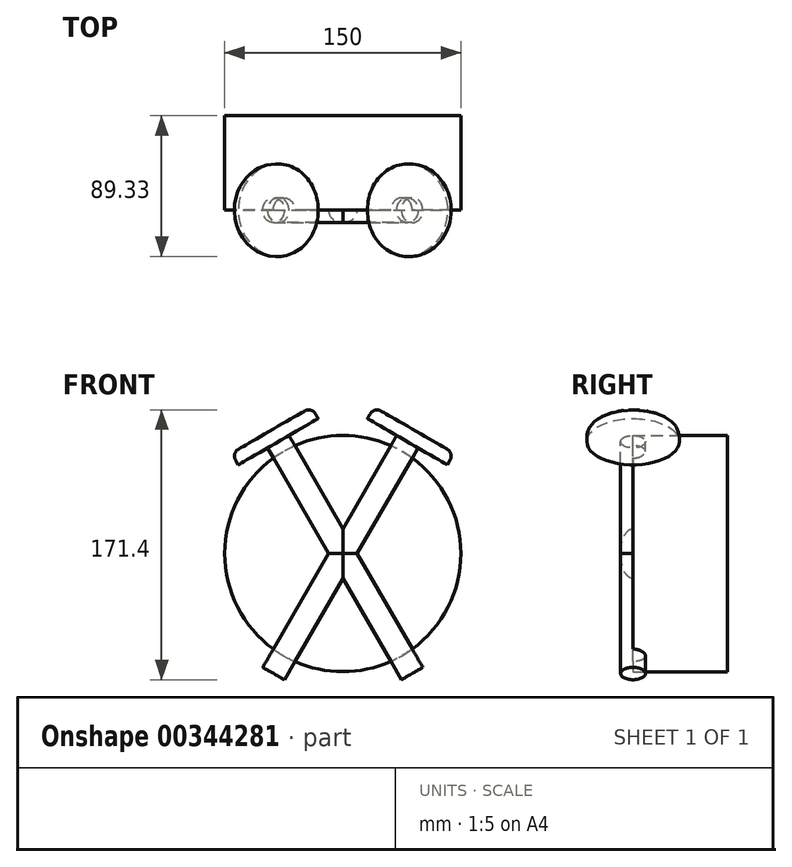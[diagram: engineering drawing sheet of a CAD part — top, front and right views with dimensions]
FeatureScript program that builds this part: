
annotation { "Feature Type Name" : "Feature", "Feature Type Description" : "" }
export const myFeature = defineFeature(function(context is Context, id is Id, definition is map)
    precondition{}
    {
        {
            var Q0;
            Q0=qCreatedBy(makeId("Front.planeOp"),FACE);
            var sketch = newSketch(context, id + "F0", { "sketchPlane" : qUnion([Q0])});
            skCircle(sketch, "E0", {"center": v(0, 0) * mm, "radius": 75 * mm});
            skSolve(sketch);
        }
        {
            var Q0;
            Q0 = qSketchRegion(id + "F0", true);
            var Q1;
            Q1=makeQuery(id+"F0.imprint","IMPRINT",FACE,{"disambiguationData":[TD([[makeQuery(id+"F0.imprint","IMPRINT",EDGE,{"derivedFrom":sQuery(id+"F0.wireOp",EDGE,"E0")}),1.0]])]});
            extrude(context, id + "F1", {"entities" : qUnion([Q0, Q1]), "depth" : 60 * mm});
        }
        {
            var Q0;
            Q0=makeQuery(id+"F1.opExtrude","CAP_FACE",FACE,{"disambiguationData":[OSD([sQuery(id+"F0.wireOp",EDGE,"E0")])],"isStart":false});
            var sketch = newSketch(context, id + "F2", { "sketchPlane" : qUnion([Q0])});
            skCircle(sketch, "E1", {"center": v(1.94, 0) * mm, "radius": 70 * mm});
            skSolve(sketch);
        }
        {
            var Q0;
            Q0=makeQuery(id+"F2.imprint","IMPRINT",FACE,{"disambiguationData":[TD([[makeQuery(id+"F2.imprint","IMPRINT",EDGE,{"derivedFrom":sQuery(id+"F2.wireOp",EDGE,"E1")}),-1.0]])]});
            var sketch = newSketch(context, id + "F3", { "sketchPlane" : qUnion([Q0])});
            skLineSegment(sketch, "E2.bottom", {"start": v(0, 82.05) * mm, "end": v(7.89, 82.05) * mm});
            skLineSegment(sketch, "E2.top", {"start": v(0, -87.98) * mm, "end": v(7.89, -87.98) * mm});
            skLineSegment(sketch, "E2.left", {"start": v(0, 82.05) * mm, "end": v(0, -87.98) * mm});
            skLineSegment(sketch, "E2.right", {"start": v(7.89, 82.05) * mm, "end": v(7.89, -87.98) * mm});
            skLineSegment(sketch, "E3.bottom", {"start": v(0, 82.05) * mm, "end": v(29.33, 82.05) * mm});
            skLineSegment(sketch, "E3.top", {"start": v(0, 90.58) * mm, "end": v(29.33, 90.58) * mm});
            skLineSegment(sketch, "E3.left", {"start": v(0, 82.05) * mm, "end": v(0, 90.58) * mm});
            skLineSegment(sketch, "E3.right", {"start": v(29.33, 82.05) * mm, "end": v(29.33, 90.58) * mm});
            skSolve(sketch);
        }
        {
            var Q0;
            Q0 = qSketchRegion(id + "F3", true);
            var Q1;
            Q1=sQuery(id+"F3.wireOp",EDGE,"E2.left");
            revolve(context, id + "F4", {"operationType" : NewBodyOperationType.ADD, "entities" : qUnion([Q0]), "axis" : qUnion([Q1]), "revolveType" : RevolveType.FULL});
        }
        {
            var Q0;
            Q0=makeQuery(id+"F1.opExtrude","SWEPT_BODY",BODY,{"disambiguationData":[OSD([sQuery(id+"F0.wireOp",EDGE,"E0")])]});
            var Q1;
            Q1=makeQuery(id+"F1.opExtrude","CAP_EDGE",EDGE,{"disambiguationData":[OSD([sQuery(id+"F0.wireOp",EDGE,"E0")])],"isStart":true});
            transform(context, id + "F5", {"entities" : qUnion([Q0]), "transformType" : TransformType.ROTATION, "transformAxis" : qUnion([Q1]), "angle" : 30 * degree, "makeCopy" : false});
        }
        {
            var Q0;
            Q0=makeQuery(id+"F1.opExtrude","SWEPT_BODY",BODY,{"disambiguationData":[OSD([sQuery(id+"F0.wireOp",EDGE,"E0")])]});
            var Q1;
            Q1=qCreatedBy(makeId("Right.planeOp"),FACE);
            mirror(context, id + "F6", {"operationType" : NewBodyOperationType.ADD, "entities" : qUnion([Q0]), "mirrorPlane" : qUnion([Q1])});
        }
        {
            var Q0;
            Q0=makeQuery(id+"F4.opRevolve","SWEPT_EDGE",EDGE,{"disambiguationData":[OSD([sQuery(id+"F3.wireOp",EDGE,"E3.top"),sQuery(id+"F3.wireOp",EDGE,"E3.right")])]});
            fillet(context, id + "F7", {"entities" : qUnion([Q0]), "radius" : 5 * mm, "tangentPropagation" : true, "allowEdgeOverflow" : false});
        }
        {
            var Q0;
            Q0=makeQuery(id+"F6.opPattern","COPY",EDGE,{"derivedFrom":makeQuery(id+"F4.opRevolve","SWEPT_EDGE",EDGE,{"disambiguationData":[OSD([sQuery(id+"F3.wireOp",EDGE,"E3.top"),sQuery(id+"F3.wireOp",EDGE,"E3.right")])]}),"instanceName":"1"});
            fillet(context, id + "F8", {"entities" : qUnion([Q0]), "radius" : 5 * mm, "tangentPropagation" : true, "allowEdgeOverflow" : false});
        }
    });
